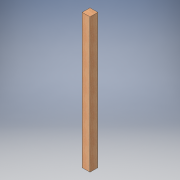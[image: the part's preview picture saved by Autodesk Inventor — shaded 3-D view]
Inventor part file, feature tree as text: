
AUTODESK INVENTOR PART (.ipt)
format: ipt  version: 2016 (Build 200138000, 138)  size: 93,696 bytes
history: native  units: in
note: dims shown in document units (in); Inventor stores cm internally (conversion verified against a paired STEP export)
features: extrude x1, sketch x1
ambient origin geometry x8: Origin, YZ Plane, XZ Plane, XY Plane, X Axis, Y Axis, Z Axis, Center Point
bodies: Solid1 (feature_tree)
feature tree (2):
  extrude  "Extrusion1"  Depth=60.0in TaperAngle=0.0deg
  sketch  "Sketch1"  dims[d0=3.5in d1=60.0in d2=0.0in]
